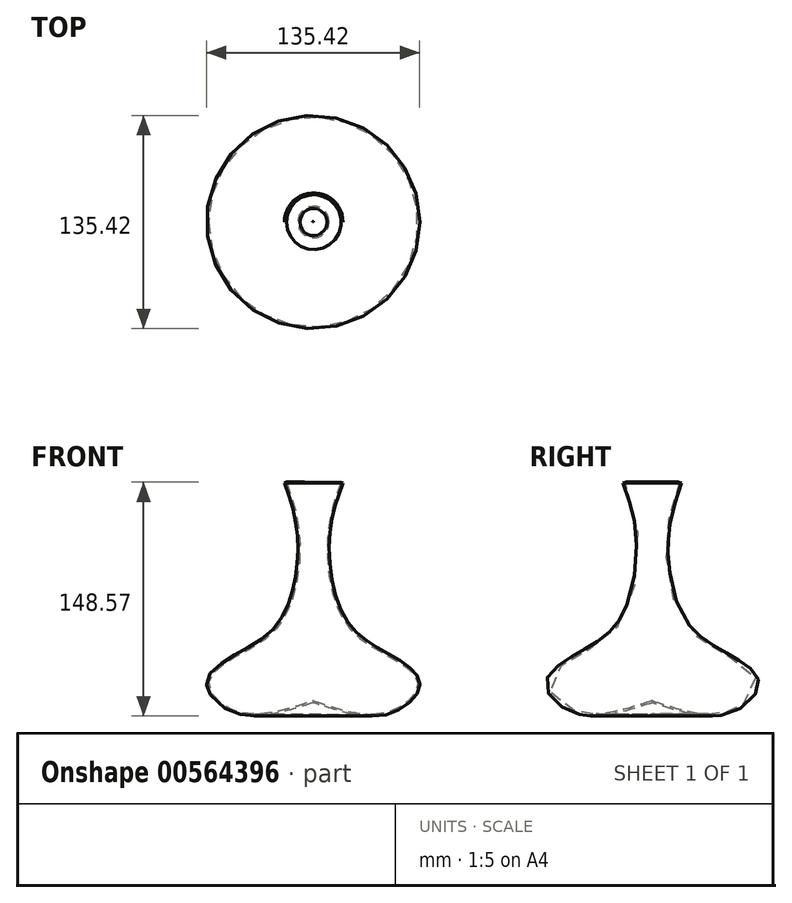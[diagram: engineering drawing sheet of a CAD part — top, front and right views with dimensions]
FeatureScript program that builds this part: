
annotation { "Feature Type Name" : "Feature", "Feature Type Description" : "" }
export const myFeature = defineFeature(function(context is Context, id is Id, definition is map)
    precondition{}
    {
        {
            var Q0;
            Q0=qCreatedBy(makeId("Front.planeOp"),FACE);
            var sketch = newSketch(context, id + "F0", { "sketchPlane" : qUnion([Q0])});
            skFitSpline(sketch, "E0", {"points": [v(18.94, 63.3) * mm, v(10.46, 28.22) * mm, v(20.78, -23.36) * mm, v(48.75, -45.6) * mm, v(67.73, -63.94) * mm, v(48.7, -83.2) * mm, v(0, -76.32) * mm], "startDerivative": vector(-69.19, -193.57) * mm, "endDerivative": vector(-269.95, 87.87) * mm});
            skFitSpline(sketch, "E1.0", {"points": [v(17.75, 63.73) * mm, v(17.03, 61.71) * mm, v(15.58, 57.67) * mm, v(13.53, 51.44) * mm, v(11.7, 44.91) * mm, v(10.48, 39.11) * mm, v(9.74, 34.2) * mm, v(9.32, 30.35) * mm, v(9.06, 26.33) * mm, v(8.92, 20.76) * mm, v(9.15, 13.5) * mm, v(10.1, 4.6) * mm, v(11.76, -4.18) * mm, v(13.75, -11.14) * mm, v(15.72, -16.34) * mm, v(17.4, -20.03) * mm, v(19.28, -23.46) * mm, v(21.38, -26.59) * mm, v(23.65, -29.42) * mm, v(26.91, -32.85) * mm, v(31.35, -36.56) * mm, v(37.08, -40.39) * mm, v(42.08, -43.29) * mm, v(46.14, -45.57) * mm, v(49.2, -47.3) * mm, v(52.25, -49.09) * mm, v(56.17, -51.52) * mm, v(59.73, -54.05) * mm, v(62.62, -56.67) * mm, v(64.37, -58.67) * mm, v(65.64, -60.69) * mm, v(66.37, -62.7) * mm, v(66.56, -64.74) * mm, v(66.18, -66.93) * mm, v(65.25, -69.22) * mm, v(63.8, -71.54) * mm, v(61.88, -73.82) * mm, v(59.56, -75.98) * mm, v(56.89, -77.97) * mm, v(53.94, -79.72) * mm, v(51.3, -80.94) * mm, v(49.11, -81.75) * mm, v(46.89, -82.42) * mm, v(44.03, -83.04) * mm, v(39.29, -83.56) * mm, v(33.07, -83.44) * mm, v(25.24, -82.27) * mm, v(17.13, -80.32) * mm, v(8.82, -77.85) * mm, v(3.2, -76.02) * mm, v(0.4, -75.1) * mm]});
            skLineSegment(sketch, "E2", {"start": v(17.75, 63.73) * mm, "end": v(18.94, 63.3) * mm});
            skLineSegment(sketch, "E3", {"start": v(0, -76.32) * mm, "end": v(0, -75.1) * mm});
            skLineSegment(sketch, "E4", {"start": v(0, -75.1) * mm, "end": v(0.4, -75.1) * mm});
            skLineSegment(sketch, "E5", {"start": v(0, -76.32) * mm, "end": v(0.4, 63.28) * mm});
            skSolve(sketch);
        }
        {
            var Q0;
            {var subQ4=sQuery(id+"F0.wireOp",EDGE,"E0");Q0=makeQuery(id+"F0.imprint","IMPRINT",FACE,{"disambiguationData":[TD([[makeQuery(id+"F0.imprint","IMPRINT",EDGE,{"derivedFrom":subQ4}),-1.0]])]});}
            var Q1;
            Q1=sQuery(id+"F0.wireOp",EDGE,"E5");
            revolve(context, id + "F1", {"entities" : qUnion([Q0]), "axis" : qUnion([Q1]), "revolveType" : RevolveType.FULL});
        }
    });
